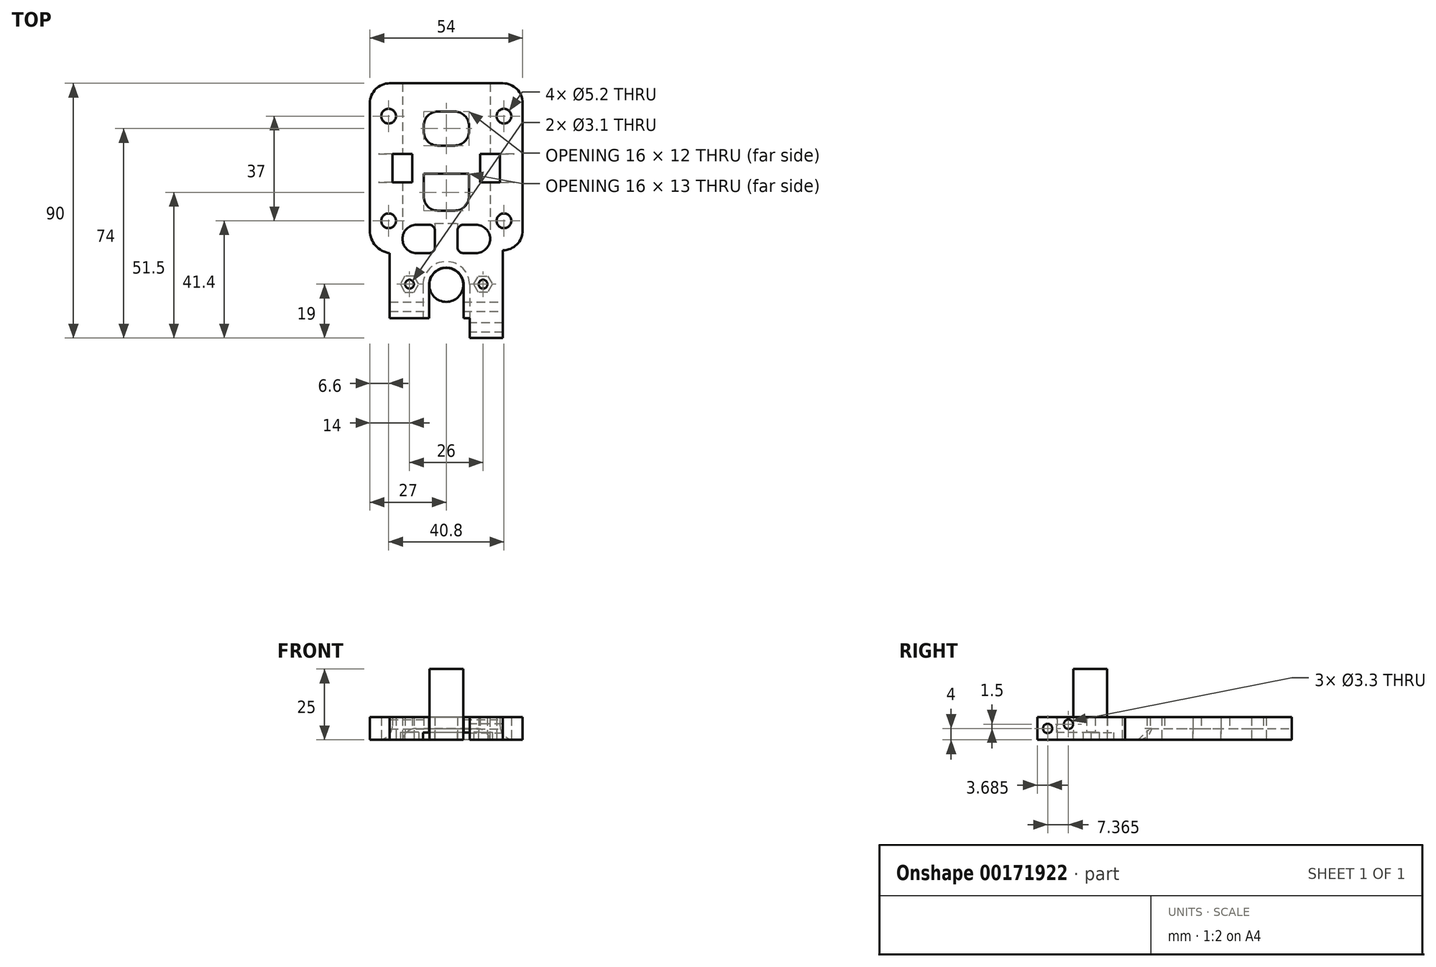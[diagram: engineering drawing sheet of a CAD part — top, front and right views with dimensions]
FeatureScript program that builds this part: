
annotation { "Feature Type Name" : "Feature", "Feature Type Description" : "" }
export const myFeature = defineFeature(function(context is Context, id is Id, definition is map)
    precondition{}
    {
        {
            var Q0;
            Q0=qCreatedBy(makeId("Top.planeOp"),FACE);
            var sketch = newSketch(context, id + "F0", { "sketchPlane" : qUnion([Q0])});
            skLineSegment(sketch, "E0.bottom", {"start": v(-27, 42.5) * mm, "end": v(27, 42.5) * mm});
            skLineSegment(sketch, "E0.top", {"start": v(-20, -42.5) * mm, "end": v(-6.1, -42.5) * mm});
            skLineSegment(sketch, "E0.left", {"start": v(-27, 42.5) * mm, "end": v(-27, -26.5) * mm});
            skLineSegment(sketch, "E0.right", {"start": v(27, 42.5) * mm, "end": v(27, -16.5) * mm});
            skPoint(sketch, "E0.middle", {"position": v(0, 0) * mm});
            skLineSegment(sketch, "E1.left", {"start": v(-20, -26.5) * mm, "end": v(-20, -42.5) * mm});
            skLineSegment(sketch, "E1.right", {"start": v(20, -16.5) * mm, "end": v(20, -42.5) * mm});
            skLineSegment(sketch, "E2", {"start": v(-20, -26.5) * mm, "end": v(-27, -26.5) * mm});
            skPoint(sketch, "E3.orphan", {"position": v(-27, -42.5) * mm});
            skLineSegment(sketch, "E4", {"start": v(20, -16.5) * mm, "end": v(27, -16.5) * mm});
            skPoint(sketch, "E5.orphan", {"position": v(27, -42.5) * mm});
            skCircle(sketch, "E6", {"center": v(-20.4, 30.9) * mm, "radius": 2.6 * mm});
            skCircle(sketch, "E7", {"center": v(-20.4, -6.1) * mm, "radius": 2.6 * mm});
            skCircle(sketch, "E8", {"center": v(20.4, 30.9) * mm, "radius": 2.6 * mm});
            skCircle(sketch, "E9.MirrorC", {"center": v(20.4, -6.1) * mm, "radius": 2.6 * mm});
            skLineSegment(sketch, "E10.bottom", {"start": v(-19, 17.5) * mm, "end": v(-12, 17.5) * mm});
            skLineSegment(sketch, "E10.top", {"start": v(-19, 7.5) * mm, "end": v(-12, 7.5) * mm});
            skLineSegment(sketch, "E10.left", {"start": v(-19, 17.5) * mm, "end": v(-19, 7.5) * mm});
            skLineSegment(sketch, "E10.right", {"start": v(-12, 17.5) * mm, "end": v(-12, 7.5) * mm});
            skLineSegment(sketch, "E11.MirrorCS", {"start": v(12, 17.5) * mm, "end": v(12, 7.5) * mm});
            skLineSegment(sketch, "E12.MirrorCS", {"start": v(19, 7.5) * mm, "end": v(12, 7.5) * mm});
            skLineSegment(sketch, "E13.MirrorCS", {"start": v(19, 17.5) * mm, "end": v(19, 7.5) * mm});
            skLineSegment(sketch, "E14.MirrorCS", {"start": v(19, 17.5) * mm, "end": v(12, 17.5) * mm});
            skEllipse(sketch, "E15", {"center": v(0, -13) * mm, "majorRadius": 7.5 * mm, "minorRadius": 4.5 * mm, "majorAxis": v(1, 0)});
            skArc(sketch, "E16", {"start": v(6.1, -28.75) * mm, "mid": v(0, -22.65) * mm, "end": v(-6.1, -28.75) * mm});
            skCircle(sketch, "E17", {"center": v(-12.5, -13) * mm, "radius": 2 * mm});
            skLineSegment(sketch, "E18", {"start": v(-6.1, -28.75) * mm, "end": v(-6.1, -42.5) * mm});
            skLineSegment(sketch, "E19", {"start": v(6.1, -28.75) * mm, "end": v(6.1, -42.5) * mm});
            skLineSegment(sketch, "E20.trimOffspring", {"start": v(6.1, -42.5) * mm, "end": v(20, -42.5) * mm});
            skArc(sketch, "E21", {"start": v(6.1, -34.3) * mm, "mid": v(0, -20.5) * mm, "end": v(-6.1, -34.3) * mm});
            skCircle(sketch, "E22", {"center": v(0, -28.75) * mm, "radius": 6 * mm});
            skSolve(sketch);
        }
        {
            var Q0;
            {var subQ0=sQuery(id+"F0.wireOp",EDGE,"E16");Q0=makeQuery(id+"F0.imprint","IMPRINT",FACE,{"disambiguationData":[TD([[makeQuery(id+"F0.imprint","IMPRINT",EDGE,{"derivedFrom":subQ0}),-1.0]])]});}
            var Q1;
            Q1=makeQuery(id+"F0.imprint","IMPRINT",FACE,{"disambiguationData":[TD([[makeQuery(id+"F0.imprint","IMPRINT",EDGE,{"derivedFrom":sQuery(id+"F0.wireOp",EDGE,"E0.bottom")}),-1.0]])]});
            extrude(context, id + "F1", {"entities" : qUnion([Q0, Q1]), "depth" : 8 * mm});
        }
        {
            var Q0;
            {var subQ0=sQuery(id+"F0.wireOp",EDGE,"E16");Q0=makeQuery(id+"F0.imprint","IMPRINT",FACE,{"disambiguationData":[TD([[makeQuery(id+"F0.imprint","IMPRINT",EDGE,{"derivedFrom":subQ0}),-1.0]])]});}
            extrude(context, id + "F2", {"entities" : qUnion([Q0]), "operationType" : NewBodyOperationType.REMOVE, "depth" : 2.6 * mm});
        }
        {
            var Q0;
            Q0=makeQuery(id+"F0.imprint","IMPRINT",FACE,{"disambiguationData":[TD([[makeQuery(id+"F0.imprint","IMPRINT",EDGE,{"derivedFrom":sQuery(id+"F0.wireOp",EDGE,"E22")}),1.0]])]});
            extrude(context, id + "F3", {"entities" : qUnion([Q0]), "depth" : 25 * mm});
        }
        {
            var Q0;
            Q0=qCreatedBy(makeId("Right.planeOp"),FACE);
            var sketch = newSketch(context, id + "F4", { "sketchPlane" : qUnion([Q0])});
            skCircle(sketch, "E23", {"center": v(-36.45, 5.5) * mm, "radius": 1.65 * mm});
            skLineSegment(sketch, "E24", {"start": v(-34.74, 0) * mm, "end": v(-34.74, 1.48) * mm});
            skSolve(sketch);
        }
        {
            var Q0;
            Q0=makeQuery(id+"F4.imprint","IMPRINT",FACE,{"disambiguationData":[TD([[makeQuery(id+"F4.imprint","IMPRINT",EDGE,{"derivedFrom":sQuery(id+"F4.wireOp",EDGE,"E23")}),1.0]])]});
            extrude(context, id + "F5", {"entities" : qUnion([Q0]), "operationType" : NewBodyOperationType.REMOVE, "endBound" : BoundingType.SYMMETRIC, "oppositeDirection" : true, "depth" : 100 * mm});
        }
        {
            var Q0;
            Q0=makeQuery(id+"F1.opExtrude","SWEPT_FACE",FACE,{"disambiguationData":[OSD([sQuery(id+"F0.wireOp",EDGE,"E20.trimOffspring")])]});
            extrude(context, id + "F6", {"entities" : qUnion([Q0]), "operationType" : NewBodyOperationType.ADD, "depth" : 5 * mm});
        }
        {
            var Q0;
            Q0=makeQuery(id+"F1.opExtrude","SWEPT_FACE",FACE,{"disambiguationData":[OSD([sQuery(id+"F0.wireOp",EDGE,"E0.top")])]});
            extrude(context, id + "F7", {"entities" : qUnion([Q0]), "operationType" : NewBodyOperationType.REMOVE, "oppositeDirection" : true, "depth" : 2 * mm});
        }
        {
            var Q0;
            {var subQ0=sQuery(id+"F0.wireOp",EDGE,"E20.trimOffspring");Q0=makeQuery(id+"F6.boolean.opBoolean","MERGE",FACE,{"derivedFrom":[makeQuery(id+"F1.opExtrude","CAP_FACE",FACE,{"disambiguationData":[OSD([sQuery(id+"F0.wireOp",EDGE,"E0.bottom"),sQuery(id+"F0.wireOp",EDGE,"E0.left"),sQuery(id+"F0.wireOp",EDGE,"E0.right"),sQuery(id+"F0.wireOp",EDGE,"E0.top"),sQuery(id+"F0.wireOp",EDGE,"E1.left"),sQuery(id+"F0.wireOp",EDGE,"E1.right"),sQuery(id+"F0.wireOp",EDGE,"E2"),sQuery(id+"F0.wireOp",EDGE,"E4"),sQuery(id+"F0.wireOp",EDGE,"E6"),sQuery(id+"F0.wireOp",EDGE,"E7"),sQuery(id+"F0.wireOp",EDGE,"E8"),sQuery(id+"F0.wireOp",EDGE,"E9.MirrorC"),sQuery(id+"F0.wireOp",EDGE,"E10.bottom"),sQuery(id+"F0.wireOp",EDGE,"E10.top"),sQuery(id+"F0.wireOp",EDGE,"E10.left"),sQuery(id+"F0.wireOp",EDGE,"E10.right"),sQuery(id+"F0.wireOp",EDGE,"E11.MirrorCS"),sQuery(id+"F0.wireOp",EDGE,"E12.MirrorCS"),sQuery(id+"F0.wireOp",EDGE,"E13.MirrorCS"),sQuery(id+"F0.wireOp",EDGE,"E14.MirrorCS"),sQuery(id+"F0.wireOp",EDGE,"E15"),sQuery(id+"F0.wireOp",EDGE,"E16"),sQuery(id+"F0.wireOp",EDGE,"E17"),sQuery(id+"F0.wireOp",EDGE,"E18"),sQuery(id+"F0.wireOp",EDGE,"E19"),subQ0])],"isStart":true}),makeQuery(id+"F6.opExtrude","SWEPT_FACE",FACE,{"disambiguationData":[OSD([subQ0]),TDD([makeQuery(id+"F1.opExtrude","CAP_EDGE",EDGE,{"disambiguationData":[OSD([subQ0])],"isStart":true})])]})]});}
            var sketch = newSketch(context, id + "F8", { "sketchPlane" : qUnion([Q0])});
            skLineSegment(sketch, "E25", {"start": v(8.25, 28.75) * mm, "end": v(8.25, 47.5) * mm});
            skLineSegment(sketch, "E26", {"start": v(-8.25, 28.75) * mm, "end": v(-8.25, 40.5) * mm});
            skLineSegment(sketch, "E27", {"start": v(0, 28.75) * mm, "end": v(8.25, 28.75) * mm});
            skLineSegment(sketch, "E28", {"start": v(0, 28.75) * mm, "end": v(-8.25, 28.75) * mm});
            skSolve(sketch);
        }
        {
            var Q0;
            {var subQ0=sQuery(id+"F8.wireOp",EDGE,"E25");Q0=makeQuery(id+"F8.imprint","IMPRINT",FACE,{"disambiguationData":[TD([[makeQuery(id+"F8.imprint","IMPRINT",EDGE,{"derivedFrom":subQ0}),1.0]])]});}
            var Q1;
            {var subQ0=sQuery(id+"F8.wireOp",EDGE,"E26");Q1=makeQuery(id+"F8.imprint","IMPRINT",FACE,{"disambiguationData":[TD([[makeQuery(id+"F8.imprint","IMPRINT",EDGE,{"derivedFrom":subQ0}),-1.0]])]});}
            var Q2;
            Q2=makeQuery(id+"F2.boolean.opBoolean","COPY",FACE,{"derivedFrom":makeQuery(id+"F2.opExtrude","CAP_FACE",FACE,{"disambiguationData":[OSD([sQuery(id+"F0.wireOp",EDGE,"E16"),sQuery(id+"F0.wireOp",EDGE,"E18"),sQuery(id+"F0.wireOp",EDGE,"E19"),sQuery(id+"F0.wireOp",EDGE,"E21")])],"isStart":false})});
            extrude(context, id + "F9", {"entities" : qUnion([Q0, Q1]), "operationType" : NewBodyOperationType.REMOVE, "endBound" : BoundingType.UP_TO_SURFACE, "oppositeDirection" : true, "endBoundEntityFace" : qUnion([Q2]), "depth" : 25 * mm});
        }
        {
            var Q0;
            {var subQ0=sQuery(id+"F0.wireOp",EDGE,"E19");Q0=makeQuery(id+"F6.boolean.opBoolean","MERGE",FACE,{"derivedFrom":[makeQuery(id+"F1.opExtrude","SWEPT_FACE",FACE,{"disambiguationData":[OSD([subQ0])]}),makeQuery(id+"F6.opExtrude","SWEPT_FACE",FACE,{"disambiguationData":[OSD([subQ0,sQuery(id+"F0.wireOp",EDGE,"E20.trimOffspring")])]})]});}
            var sketch = newSketch(context, id + "F10", { "sketchPlane" : qUnion([Q0])});
            skLineSegment(sketch, "E29.bottom", {"start": v(47.5, 2.6) * mm, "end": v(40.53, 2.6) * mm});
            skLineSegment(sketch, "E29.top", {"start": v(47.5, 8) * mm, "end": v(40.53, 8) * mm});
            skLineSegment(sketch, "E29.left", {"start": v(47.5, 2.6) * mm, "end": v(47.5, 8) * mm});
            skLineSegment(sketch, "E29.right", {"start": v(40.53, 2.6) * mm, "end": v(40.53, 8) * mm});
            skSolve(sketch);
        }
        {
            var Q0;
            Q0 = qSketchRegion(id + "F10", true);
            var Q1;
            Q1=makeQuery(id+"F9.boolean.opBoolean","COPY",FACE,{"derivedFrom":makeQuery(id+"F9.opExtrude","SWEPT_FACE",FACE,{"disambiguationData":[OSD([sQuery(id+"F8.wireOp",EDGE,"E25")])]})});
            extrude(context, id + "F11", {"entities" : qUnion([Q0]), "operationType" : NewBodyOperationType.REMOVE, "endBound" : BoundingType.UP_TO_SURFACE, "oppositeDirection" : true, "endBoundEntityFace" : qUnion([Q1]), "depth" : 25 * mm});
        }
        {
            var Q0;
            Q0=makeQuery(id+"F11.boolean.opBoolean","MERGE",FACE,{"derivedFrom":[makeQuery(id+"F9.boolean.opBoolean","COPY",FACE,{"derivedFrom":makeQuery(id+"F9.opExtrude","SWEPT_FACE",FACE,{"disambiguationData":[OSD([sQuery(id+"F8.wireOp",EDGE,"E25")])]})})],"fromTools":[makeQuery(id+"F11.opExtrude","CAP_FACE",FACE,{"disambiguationData":[OSD([sQuery(id+"F10.wireOp",EDGE,"E29.bottom"),sQuery(id+"F10.wireOp",EDGE,"E29.top"),sQuery(id+"F10.wireOp",EDGE,"E29.left"),sQuery(id+"F10.wireOp",EDGE,"E29.right")])],"isStart":false})]});
            var sketch = newSketch(context, id + "F12", { "sketchPlane" : qUnion([Q0])});
            skCircle(sketch, "E30", {"center": v(43.82, 4) * mm, "radius": 1.65 * mm});
            skPoint(sketch, "E30.centerSnap0", {"position": v(47.5, 4) * mm});
            skSolve(sketch);
        }
        {
            var Q0;
            Q0=makeQuery(id+"F12.imprint","IMPRINT",FACE,{"disambiguationData":[TD([[makeQuery(id+"F12.imprint","IMPRINT",EDGE,{"derivedFrom":sQuery(id+"F12.wireOp",EDGE,"E30")}),1.0]])]});
            extrude(context, id + "F13", {"entities" : qUnion([Q0]), "operationType" : NewBodyOperationType.REMOVE, "oppositeDirection" : true, "depth" : 25 * mm});
        }
        {
            var Q0;
            {var subQ0=sQuery(id+"F0.wireOp",EDGE,"E20.trimOffspring");Q0=makeQuery(id+"F6.boolean.opBoolean","MERGE",FACE,{"derivedFrom":[makeQuery(id+"F1.opExtrude","CAP_FACE",FACE,{"disambiguationData":[OSD([sQuery(id+"F0.wireOp",EDGE,"E0.bottom"),sQuery(id+"F0.wireOp",EDGE,"E0.left"),sQuery(id+"F0.wireOp",EDGE,"E0.right"),sQuery(id+"F0.wireOp",EDGE,"E0.top"),sQuery(id+"F0.wireOp",EDGE,"E1.left"),sQuery(id+"F0.wireOp",EDGE,"E1.right"),sQuery(id+"F0.wireOp",EDGE,"E2"),sQuery(id+"F0.wireOp",EDGE,"E4"),sQuery(id+"F0.wireOp",EDGE,"E6"),sQuery(id+"F0.wireOp",EDGE,"E7"),sQuery(id+"F0.wireOp",EDGE,"E8"),sQuery(id+"F0.wireOp",EDGE,"E9.MirrorC"),sQuery(id+"F0.wireOp",EDGE,"E10.bottom"),sQuery(id+"F0.wireOp",EDGE,"E10.top"),sQuery(id+"F0.wireOp",EDGE,"E10.left"),sQuery(id+"F0.wireOp",EDGE,"E10.right"),sQuery(id+"F0.wireOp",EDGE,"E11.MirrorCS"),sQuery(id+"F0.wireOp",EDGE,"E12.MirrorCS"),sQuery(id+"F0.wireOp",EDGE,"E13.MirrorCS"),sQuery(id+"F0.wireOp",EDGE,"E14.MirrorCS"),sQuery(id+"F0.wireOp",EDGE,"E15"),sQuery(id+"F0.wireOp",EDGE,"E16"),sQuery(id+"F0.wireOp",EDGE,"E17"),sQuery(id+"F0.wireOp",EDGE,"E18"),sQuery(id+"F0.wireOp",EDGE,"E19"),subQ0])],"isStart":true}),makeQuery(id+"F6.opExtrude","SWEPT_FACE",FACE,{"disambiguationData":[OSD([subQ0]),TDD([makeQuery(id+"F1.opExtrude","CAP_EDGE",EDGE,{"disambiguationData":[OSD([subQ0])],"isStart":true})])]})]});}
            var sketch = newSketch(context, id + "F14", { "sketchPlane" : qUnion([Q0])});
            skCircle(sketch, "E31.cCircle", {"center": v(-13, 28.5) * mm, "radius": 2.85 * mm, "construction": true});
            skLineSegment(sketch, "E31.0", {"start": v(-11.35, 25.65) * mm, "end": v(-14.65, 25.65) * mm});
            skLineSegment(sketch, "E31.1", {"start": v(-14.65, 25.65) * mm, "end": v(-16.3, 28.5) * mm});
            skLineSegment(sketch, "E31.2", {"start": v(-16.3, 28.5) * mm, "end": v(-14.65, 31.35) * mm});
            skLineSegment(sketch, "E31.3", {"start": v(-14.65, 31.35) * mm, "end": v(-11.35, 31.35) * mm});
            skLineSegment(sketch, "E31.4", {"start": v(-11.35, 31.35) * mm, "end": v(-9.7, 28.5) * mm});
            skLineSegment(sketch, "E31.5", {"start": v(-9.7, 28.5) * mm, "end": v(-11.35, 25.65) * mm});
            skPoint(sketch, "E31.0.midPoint", {"position": v(-13, 25.65) * mm});
            skLineSegment(sketch, "E32.MirrorCS", {"start": v(9.7, 28.5) * mm, "end": v(11.35, 25.65) * mm});
            skLineSegment(sketch, "E33.MirrorCS", {"start": v(11.35, 31.35) * mm, "end": v(9.7, 28.5) * mm});
            skLineSegment(sketch, "E34.MirrorCS", {"start": v(14.65, 31.35) * mm, "end": v(11.35, 31.35) * mm});
            skPoint(sketch, "E35.MirrorP", {"position": v(13, 25.65) * mm});
            skCircle(sketch, "E36.MirrorC", {"center": v(13, 28.5) * mm, "radius": 2.85 * mm, "construction": true});
            skLineSegment(sketch, "E37.MirrorCS", {"start": v(11.35, 25.65) * mm, "end": v(14.65, 25.65) * mm});
            skLineSegment(sketch, "E38.MirrorCS", {"start": v(14.65, 25.65) * mm, "end": v(16.3, 28.5) * mm});
            skLineSegment(sketch, "E39.MirrorCS", {"start": v(16.3, 28.5) * mm, "end": v(14.65, 31.35) * mm});
            skCircle(sketch, "E40", {"center": v(-13, 28.5) * mm, "radius": 1.55 * mm});
            skCircle(sketch, "E41.MirrorC", {"center": v(13, 28.5) * mm, "radius": 1.55 * mm});
            skSolve(sketch);
        }
        {
            var Q0;
            Q0 = qSketchRegion(id + "F14", true);
            extrude(context, id + "F15", {"entities" : qUnion([Q0]), "operationType" : NewBodyOperationType.REMOVE, "oppositeDirection" : true, "depth" : 2.7 * mm});
        }
        {
            var Q0;
            {var subQ0=sQuery(id+"F0.wireOp",EDGE,"E20.trimOffspring");Q0=makeQuery(id+"F15.boolean.opBoolean","SPLIT",FACE,{"disambiguationData":[TD([makeQuery(id+"F15.opExtrude","SWEPT_FACE",FACE,{"disambiguationData":[OSD([sQuery(id+"F14.wireOp",EDGE,"E40")])]})])],"derivedFrom":makeQuery(id+"F6.boolean.opBoolean","MERGE",FACE,{"derivedFrom":[makeQuery(id+"F1.opExtrude","CAP_FACE",FACE,{"disambiguationData":[OSD([sQuery(id+"F0.wireOp",EDGE,"E0.bottom"),sQuery(id+"F0.wireOp",EDGE,"E0.left"),sQuery(id+"F0.wireOp",EDGE,"E0.right"),sQuery(id+"F0.wireOp",EDGE,"E0.top"),sQuery(id+"F0.wireOp",EDGE,"E1.left"),sQuery(id+"F0.wireOp",EDGE,"E1.right"),sQuery(id+"F0.wireOp",EDGE,"E2"),sQuery(id+"F0.wireOp",EDGE,"E4"),sQuery(id+"F0.wireOp",EDGE,"E6"),sQuery(id+"F0.wireOp",EDGE,"E7"),sQuery(id+"F0.wireOp",EDGE,"E8"),sQuery(id+"F0.wireOp",EDGE,"E9.MirrorC"),sQuery(id+"F0.wireOp",EDGE,"E10.bottom"),sQuery(id+"F0.wireOp",EDGE,"E10.top"),sQuery(id+"F0.wireOp",EDGE,"E10.left"),sQuery(id+"F0.wireOp",EDGE,"E10.right"),sQuery(id+"F0.wireOp",EDGE,"E11.MirrorCS"),sQuery(id+"F0.wireOp",EDGE,"E12.MirrorCS"),sQuery(id+"F0.wireOp",EDGE,"E13.MirrorCS"),sQuery(id+"F0.wireOp",EDGE,"E14.MirrorCS"),sQuery(id+"F0.wireOp",EDGE,"E15"),sQuery(id+"F0.wireOp",EDGE,"E16"),sQuery(id+"F0.wireOp",EDGE,"E17"),sQuery(id+"F0.wireOp",EDGE,"E18"),sQuery(id+"F0.wireOp",EDGE,"E19"),subQ0])],"isStart":true}),makeQuery(id+"F6.opExtrude","SWEPT_FACE",FACE,{"disambiguationData":[OSD([subQ0]),TDD([makeQuery(id+"F1.opExtrude","CAP_EDGE",EDGE,{"disambiguationData":[OSD([subQ0])],"isStart":true})])]})]})});}
            var Q1;
            {var subQ0=sQuery(id+"F0.wireOp",EDGE,"E20.trimOffspring");Q1=makeQuery(id+"F15.boolean.opBoolean","SPLIT",FACE,{"disambiguationData":[TD([makeQuery(id+"F15.opExtrude","SWEPT_FACE",FACE,{"disambiguationData":[OSD([sQuery(id+"F14.wireOp",EDGE,"E41.MirrorC")])]})])],"derivedFrom":makeQuery(id+"F6.boolean.opBoolean","MERGE",FACE,{"derivedFrom":[makeQuery(id+"F1.opExtrude","CAP_FACE",FACE,{"disambiguationData":[OSD([sQuery(id+"F0.wireOp",EDGE,"E0.bottom"),sQuery(id+"F0.wireOp",EDGE,"E0.left"),sQuery(id+"F0.wireOp",EDGE,"E0.right"),sQuery(id+"F0.wireOp",EDGE,"E0.top"),sQuery(id+"F0.wireOp",EDGE,"E1.left"),sQuery(id+"F0.wireOp",EDGE,"E1.right"),sQuery(id+"F0.wireOp",EDGE,"E2"),sQuery(id+"F0.wireOp",EDGE,"E4"),sQuery(id+"F0.wireOp",EDGE,"E6"),sQuery(id+"F0.wireOp",EDGE,"E7"),sQuery(id+"F0.wireOp",EDGE,"E8"),sQuery(id+"F0.wireOp",EDGE,"E9.MirrorC"),sQuery(id+"F0.wireOp",EDGE,"E10.bottom"),sQuery(id+"F0.wireOp",EDGE,"E10.top"),sQuery(id+"F0.wireOp",EDGE,"E10.left"),sQuery(id+"F0.wireOp",EDGE,"E10.right"),sQuery(id+"F0.wireOp",EDGE,"E11.MirrorCS"),sQuery(id+"F0.wireOp",EDGE,"E12.MirrorCS"),sQuery(id+"F0.wireOp",EDGE,"E13.MirrorCS"),sQuery(id+"F0.wireOp",EDGE,"E14.MirrorCS"),sQuery(id+"F0.wireOp",EDGE,"E15"),sQuery(id+"F0.wireOp",EDGE,"E16"),sQuery(id+"F0.wireOp",EDGE,"E17"),sQuery(id+"F0.wireOp",EDGE,"E18"),sQuery(id+"F0.wireOp",EDGE,"E19"),subQ0])],"isStart":true}),makeQuery(id+"F6.opExtrude","SWEPT_FACE",FACE,{"disambiguationData":[OSD([subQ0]),TDD([makeQuery(id+"F1.opExtrude","CAP_EDGE",EDGE,{"disambiguationData":[OSD([subQ0])],"isStart":true})])]})]})});}
            extrude(context, id + "F16", {"entities" : qUnion([Q0, Q1]), "operationType" : NewBodyOperationType.REMOVE, "oppositeDirection" : true, "depth" : 25 * mm});
        }
        {
            var Q0;
            Q0=makeQuery(id+"F1.opExtrude","SWEPT_EDGE",EDGE,{"disambiguationData":[OSD([sQuery(id+"F0.wireOp",EDGE,"E0.bottom"),sQuery(id+"F0.wireOp",EDGE,"E0.right")])]});
            var Q1;
            Q1=makeQuery(id+"F1.opExtrude","SWEPT_EDGE",EDGE,{"disambiguationData":[OSD([sQuery(id+"F0.wireOp",EDGE,"E0.bottom"),sQuery(id+"F0.wireOp",EDGE,"E0.left")])]});
            var Q2;
            Q2=makeQuery(id+"F1.opExtrude","SWEPT_EDGE",EDGE,{"disambiguationData":[OSD([sQuery(id+"F0.wireOp",EDGE,"E0.left"),sQuery(id+"F0.wireOp",EDGE,"E2")])]});
            var Q3;
            Q3=makeQuery(id+"F1.opExtrude","SWEPT_EDGE",EDGE,{"disambiguationData":[OSD([sQuery(id+"F0.wireOp",EDGE,"E0.right"),sQuery(id+"F0.wireOp",EDGE,"E4")])]});
            fillet(context, id + "F17", {"entities" : qUnion([Q0, Q1, Q2, Q3]), "radius" : 7 * mm, "tangentPropagation" : true, "allowEdgeOverflow" : false});
        }
        {
            var Q0;
            {var subQ0=sQuery(id+"F0.wireOp",EDGE,"E17");var subQ1=sQuery(id+"F0.wireOp",EDGE,"E15");var subQ2=sQuery(id+"F0.wireOp",EDGE,"E14.MirrorCS");var subQ3=sQuery(id+"F0.wireOp",EDGE,"E13.MirrorCS");var subQ4=sQuery(id+"F0.wireOp",EDGE,"E0.right");var subQ5=sQuery(id+"F0.wireOp",EDGE,"E12.MirrorCS");var subQ6=sQuery(id+"F0.wireOp",EDGE,"E11.MirrorCS");var subQ7=sQuery(id+"F0.wireOp",EDGE,"E0.top");var subQ8=sQuery(id+"F0.wireOp",EDGE,"E10.right");var subQ9=sQuery(id+"F0.wireOp",EDGE,"E10.left");var subQ10=sQuery(id+"F0.wireOp",EDGE,"E10.top");var subQ11=sQuery(id+"F0.wireOp",EDGE,"E10.bottom");var subQ12=sQuery(id+"F0.wireOp",EDGE,"E9.MirrorC");var subQ13=sQuery(id+"F0.wireOp",EDGE,"E1.left");var subQ14=sQuery(id+"F0.wireOp",EDGE,"E0.left");var subQ15=sQuery(id+"F0.wireOp",EDGE,"E0.bottom");var subQ16=sQuery(id+"F0.wireOp",EDGE,"E7");var subQ17=sQuery(id+"F0.wireOp",EDGE,"E1.right");var subQ18=sQuery(id+"F0.wireOp",EDGE,"E2");var subQ19=sQuery(id+"F0.wireOp",EDGE,"E4");var subQ20=sQuery(id+"F0.wireOp",EDGE,"E6");var subQ21=sQuery(id+"F0.wireOp",EDGE,"E8");var subQ22=sQuery(id+"F0.wireOp",EDGE,"E20.trimOffspring");Q0=makeQuery(id+"F15.boolean.opBoolean","SPLIT",FACE,{"disambiguationData":[TD([makeQuery(id+"F1.opExtrude","SWEPT_FACE",FACE,{"disambiguationData":[OSD([subQ15])]})])],"derivedFrom":makeQuery(id+"F6.boolean.opBoolean","MERGE",FACE,{"derivedFrom":[makeQuery(id+"F1.opExtrude","CAP_FACE",FACE,{"disambiguationData":[OSD([subQ15,subQ14,subQ4,subQ7,subQ13,subQ17,subQ18,subQ19,subQ20,subQ16,subQ21,subQ12,subQ11,subQ10,subQ9,subQ8,subQ6,subQ5,subQ3,subQ2,subQ1,sQuery(id+"F0.wireOp",EDGE,"E16"),subQ0,sQuery(id+"F0.wireOp",EDGE,"E18"),sQuery(id+"F0.wireOp",EDGE,"E19"),subQ22])],"isStart":true}),makeQuery(id+"F6.opExtrude","SWEPT_FACE",FACE,{"disambiguationData":[OSD([subQ22]),TDD([makeQuery(id+"F1.opExtrude","CAP_EDGE",EDGE,{"disambiguationData":[OSD([subQ22])],"isStart":true})])]})]})});}
            var sketch = newSketch(context, id + "F18", { "sketchPlane" : qUnion([Q0])});
            skLineSegment(sketch, "E42.bottom", {"start": v(8, -32.5) * mm, "end": v(-8, -32.5) * mm});
            skLineSegment(sketch, "E42.top", {"start": v(8, 2.5) * mm, "end": v(-8, 2.5) * mm});
            skLineSegment(sketch, "E42.left", {"start": v(8, -32.5) * mm, "end": v(8, 2.5) * mm});
            skLineSegment(sketch, "E42.right", {"start": v(-8, -32.5) * mm, "end": v(-8, 2.5) * mm});
            skPoint(sketch, "E42.middle", {"position": v(0, -15) * mm});
            skSolve(sketch);
        }
        {
            var Q0;
            Q0 = qSketchRegion(id + "F18", true);
            extrude(context, id + "F19", {"entities" : qUnion([Q0]), "operationType" : NewBodyOperationType.REMOVE, "oppositeDirection" : true, "depth" : 25 * mm});
        }
        {
            var Q0;
            Q0=makeQuery(id+"F19.boolean.opBoolean","COPY",FACE,{"derivedFrom":makeQuery(id+"F19.opExtrude","SWEPT_FACE",FACE,{"disambiguationData":[OSD([sQuery(id+"F18.wireOp",EDGE,"E42.right")])]})});
            var sketch = newSketch(context, id + "F20", { "sketchPlane" : qUnion([Q0])});
            skLineSegment(sketch, "E43.bottom", {"start": v(10.5, 8) * mm, "end": v(20.5, 8) * mm});
            skLineSegment(sketch, "E43.top", {"start": v(10.5, 0) * mm, "end": v(20.5, 0) * mm});
            skLineSegment(sketch, "E43.left", {"start": v(10.5, 8) * mm, "end": v(10.5, 0) * mm});
            skLineSegment(sketch, "E43.right", {"start": v(20.5, 8) * mm, "end": v(20.5, 0) * mm});
            skSolve(sketch);
        }
        {
            var Q0;
            Q0 = qSketchRegion(id + "F20", true);
            extrude(context, id + "F21", {"entities" : qUnion([Q0]), "operationType" : NewBodyOperationType.ADD, "endBound" : BoundingType.UP_TO_NEXT, "depth" : 25 * mm});
        }
        {
            var Q0;
            Q0=makeQuery(id+"F21.opExtrude","CAP_EDGE",EDGE,{"disambiguationData":[OSD([sQuery(id+"F20.wireOp",EDGE,"E43.left")])],"isStart":true});
            var Q1;
            Q1=makeQuery(id+"F19.boolean.opBoolean","COPY",EDGE,{"derivedFrom":makeQuery(id+"F19.opExtrude","SWEPT_EDGE",EDGE,{"disambiguationData":[OSD([sQuery(id+"F18.wireOp",EDGE,"E42.top"),sQuery(id+"F18.wireOp",EDGE,"E42.right")])]})});
            var Q2;
            Q2=makeQuery(id+"F19.boolean.opBoolean","COPY",EDGE,{"derivedFrom":makeQuery(id+"F19.opExtrude","SWEPT_EDGE",EDGE,{"disambiguationData":[OSD([sQuery(id+"F18.wireOp",EDGE,"E42.top"),sQuery(id+"F18.wireOp",EDGE,"E42.left")])]})});
            var Q3;
            Q3=makeQuery(id+"F21.opExtrude","CAP_EDGE",EDGE,{"disambiguationData":[OSD([sQuery(id+"F20.wireOp",EDGE,"E43.left")])],"isStart":false});
            var Q4;
            Q4=makeQuery(id+"F21.opExtrude","CAP_EDGE",EDGE,{"disambiguationData":[OSD([sQuery(id+"F20.wireOp",EDGE,"E43.right")])],"isStart":false});
            var Q5;
            Q5=makeQuery(id+"F21.opExtrude","CAP_EDGE",EDGE,{"disambiguationData":[OSD([sQuery(id+"F20.wireOp",EDGE,"E43.right")])],"isStart":true});
            var Q6;
            Q6=makeQuery(id+"F19.boolean.opBoolean","COPY",EDGE,{"derivedFrom":makeQuery(id+"F19.opExtrude","SWEPT_EDGE",EDGE,{"disambiguationData":[OSD([sQuery(id+"F18.wireOp",EDGE,"E42.bottom"),sQuery(id+"F18.wireOp",EDGE,"E42.right")])]})});
            var Q7;
            Q7=makeQuery(id+"F19.boolean.opBoolean","COPY",EDGE,{"derivedFrom":makeQuery(id+"F19.opExtrude","SWEPT_EDGE",EDGE,{"disambiguationData":[OSD([sQuery(id+"F18.wireOp",EDGE,"E42.bottom"),sQuery(id+"F18.wireOp",EDGE,"E42.left")])]})});
            fillet(context, id + "F22", {"entities" : qUnion([Q0, Q1, Q2, Q3, Q4, Q5, Q6, Q7]), "radius" : 5 * mm, "tangentPropagation" : true, "allowEdgeOverflow" : false});
        }
        {
            var Q0;
            {var subQ0=sQuery(id+"F0.wireOp",EDGE,"E17");var subQ1=sQuery(id+"F0.wireOp",EDGE,"E15");var subQ2=sQuery(id+"F0.wireOp",EDGE,"E14.MirrorCS");var subQ3=sQuery(id+"F0.wireOp",EDGE,"E13.MirrorCS");var subQ4=sQuery(id+"F0.wireOp",EDGE,"E0.right");var subQ5=sQuery(id+"F0.wireOp",EDGE,"E12.MirrorCS");var subQ6=sQuery(id+"F0.wireOp",EDGE,"E11.MirrorCS");var subQ7=sQuery(id+"F0.wireOp",EDGE,"E0.top");var subQ8=sQuery(id+"F0.wireOp",EDGE,"E10.right");var subQ9=sQuery(id+"F0.wireOp",EDGE,"E10.left");var subQ10=sQuery(id+"F0.wireOp",EDGE,"E10.top");var subQ11=sQuery(id+"F0.wireOp",EDGE,"E10.bottom");var subQ12=sQuery(id+"F0.wireOp",EDGE,"E9.MirrorC");var subQ13=sQuery(id+"F0.wireOp",EDGE,"E1.left");var subQ14=sQuery(id+"F0.wireOp",EDGE,"E0.left");var subQ15=sQuery(id+"F0.wireOp",EDGE,"E0.bottom");var subQ16=sQuery(id+"F0.wireOp",EDGE,"E7");var subQ17=sQuery(id+"F0.wireOp",EDGE,"E1.right");var subQ18=sQuery(id+"F0.wireOp",EDGE,"E2");var subQ19=sQuery(id+"F0.wireOp",EDGE,"E4");var subQ20=sQuery(id+"F0.wireOp",EDGE,"E6");var subQ21=sQuery(id+"F0.wireOp",EDGE,"E8");var subQ22=sQuery(id+"F0.wireOp",EDGE,"E20.trimOffspring");Q0=makeQuery(id+"F21.boolean.opBoolean","MERGE",FACE,{"derivedFrom":[makeQuery(id+"F15.boolean.opBoolean","SPLIT",FACE,{"disambiguationData":[TD([makeQuery(id+"F1.opExtrude","SWEPT_FACE",FACE,{"disambiguationData":[OSD([subQ15])]})])],"derivedFrom":makeQuery(id+"F6.boolean.opBoolean","MERGE",FACE,{"derivedFrom":[makeQuery(id+"F1.opExtrude","CAP_FACE",FACE,{"disambiguationData":[OSD([subQ15,subQ14,subQ4,subQ7,subQ13,subQ17,subQ18,subQ19,subQ20,subQ16,subQ21,subQ12,subQ11,subQ10,subQ9,subQ8,subQ6,subQ5,subQ3,subQ2,subQ1,sQuery(id+"F0.wireOp",EDGE,"E16"),subQ0,sQuery(id+"F0.wireOp",EDGE,"E18"),sQuery(id+"F0.wireOp",EDGE,"E19"),subQ22])],"isStart":true}),makeQuery(id+"F6.opExtrude","SWEPT_FACE",FACE,{"disambiguationData":[OSD([subQ22]),TDD([makeQuery(id+"F1.opExtrude","CAP_EDGE",EDGE,{"disambiguationData":[OSD([subQ22])],"isStart":true})])]})]})}),makeQuery(id+"F21.opExtrude","SWEPT_FACE",FACE,{"disambiguationData":[OSD([sQuery(id+"F20.wireOp",EDGE,"E43.top")])]})]});}
            var sketch = newSketch(context, id + "F23", { "sketchPlane" : qUnion([Q0])});
            skPoint(sketch, "E44.oppositeSnap0", {"position": v(15.5, -7.5) * mm});
            skLineSegment(sketch, "E44.bottom", {"start": v(-15.5, -42.5) * mm, "end": v(15.5, -42.5) * mm});
            skLineSegment(sketch, "E44.top", {"start": v(-15.5, 17.5) * mm, "end": v(15.5, 17.5) * mm});
            skLineSegment(sketch, "E44.left", {"start": v(-15.5, -42.5) * mm, "end": v(-15.5, 17.5) * mm});
            skLineSegment(sketch, "E44.right", {"start": v(15.5, -42.5) * mm, "end": v(15.5, 17.5) * mm});
            skSolve(sketch);
        }
        {
            var Q0;
            Q0 = qSketchRegion(id + "F23", true);
            extrude(context, id + "F24", {"entities" : qUnion([Q0]), "operationType" : NewBodyOperationType.REMOVE, "oppositeDirection" : true, "depth" : 4 * mm});
        }
        {
            var Q0;
            Q0=makeQuery(id+"F24.boolean.opBoolean","COPY",FACE,{"derivedFrom":makeQuery(id+"F24.opExtrude","CAP_FACE",FACE,{"disambiguationData":[OSD([sQuery(id+"F23.wireOp",EDGE,"E44.bottom"),sQuery(id+"F23.wireOp",EDGE,"E44.top"),sQuery(id+"F23.wireOp",EDGE,"E44.left"),sQuery(id+"F23.wireOp",EDGE,"E44.right")])],"isStart":false})});
            var sketch = newSketch(context, id + "F25", { "sketchPlane" : qUnion([Q0])});
            skLineSegment(sketch, "E45.bottom", {"start": v(-15.5, 17.5) * mm, "end": v(15.5, 17.5) * mm});
            skLineSegment(sketch, "E45.top", {"start": v(-15.5, 7.5) * mm, "end": v(15.5, 7.5) * mm});
            skLineSegment(sketch, "E45.left", {"start": v(-15.5, 17.5) * mm, "end": v(-15.5, 7.5) * mm});
            skLineSegment(sketch, "E45.right", {"start": v(15.5, 17.5) * mm, "end": v(15.5, 7.5) * mm});
            skSolve(sketch);
        }
        {
            var Q0;
            Q0 = qSketchRegion(id + "F25", true);
            extrude(context, id + "F26", {"entities" : qUnion([Q0]), "operationType" : NewBodyOperationType.REMOVE, "oppositeDirection" : true, "depth" : 25 * mm});
        }
        {
            var Q0;
            Q0=makeQuery(id+"F1.opExtrude","CAP_EDGE",EDGE,{"disambiguationData":[OSD([sQuery(id+"F0.wireOp",EDGE,"E10.left")])],"isStart":true});
            var Q1;
            Q1=makeQuery(id+"F1.opExtrude","CAP_EDGE",EDGE,{"disambiguationData":[OSD([sQuery(id+"F0.wireOp",EDGE,"E13.MirrorCS")])],"isStart":true});
            fillet(context, id + "F27", {"entities" : qUnion([Q0, Q1]), "radius" : 5 * mm, "tangentPropagation" : true, "allowEdgeOverflow" : false});
        }
        {
            var Q0;
            {var subQ0=sQuery(id+"F23.wireOp",EDGE,"E44.left");Q0=makeQuery(id+"F24.boolean.opBoolean","COPY",EDGE,{"disambiguationData":[TD([makeQuery(id+"F1.opExtrude","SWEPT_FACE",FACE,{"disambiguationData":[OSD([sQuery(id+"F0.wireOp",EDGE,"E10.top")])]})])],"derivedFrom":makeQuery(id+"F24.opExtrude","CAP_EDGE",EDGE,{"disambiguationData":[OSD([subQ0])],"isStart":false})});}
            var Q1;
            {var subQ0=sQuery(id+"F23.wireOp",EDGE,"E44.right");Q1=makeQuery(id+"F24.boolean.opBoolean","COPY",EDGE,{"disambiguationData":[TD([makeQuery(id+"F1.opExtrude","SWEPT_FACE",FACE,{"disambiguationData":[OSD([sQuery(id+"F0.wireOp",EDGE,"E12.MirrorCS")])]})])],"derivedFrom":makeQuery(id+"F24.opExtrude","CAP_EDGE",EDGE,{"disambiguationData":[OSD([subQ0])],"isStart":false})});}
            fillet(context, id + "F28", {"entities" : qUnion([Q0, Q1]), "radius" : 5 * mm, "tangentPropagation" : true, "allowEdgeOverflow" : false});
        }
        {
            var Q0;
            Q0=makeQuery(id+"F26.boolean.opBoolean","COPY",EDGE,{"derivedFrom":makeQuery(id+"F26.opExtrude","SWEPT_EDGE",EDGE,{"disambiguationData":[OSD([sQuery(id+"F23.wireOp",EDGE,"E44.left"),sQuery(id+"F25.wireOp",EDGE,"E45.top"),sQuery(id+"F25.wireOp",EDGE,"E45.left")])]})});
            var Q1;
            Q1=makeQuery(id+"F26.boolean.opBoolean","COPY",EDGE,{"derivedFrom":makeQuery(id+"F26.opExtrude","SWEPT_EDGE",EDGE,{"disambiguationData":[OSD([sQuery(id+"F23.wireOp",EDGE,"E44.right"),sQuery(id+"F25.wireOp",EDGE,"E45.top"),sQuery(id+"F25.wireOp",EDGE,"E45.right")])]})});
            var Q2;
            Q2=makeQuery(id+"F26.boolean.opBoolean","MERGE",EDGE,{"derivedFrom":[makeQuery(id+"F24.boolean.opBoolean","COPY",EDGE,{"derivedFrom":makeQuery(id+"F24.opExtrude","SWEPT_EDGE",EDGE,{"disambiguationData":[OSD([sQuery(id+"F23.wireOp",EDGE,"E44.top"),sQuery(id+"F23.wireOp",EDGE,"E44.right")])]})}),makeQuery(id+"F26.opExtrude","SWEPT_EDGE",EDGE,{"disambiguationData":[OSD([sQuery(id+"F25.wireOp",EDGE,"E45.bottom"),sQuery(id+"F25.wireOp",EDGE,"E45.right")])]})]});
            var Q3;
            Q3=makeQuery(id+"F26.boolean.opBoolean","MERGE",EDGE,{"derivedFrom":[makeQuery(id+"F24.boolean.opBoolean","COPY",EDGE,{"derivedFrom":makeQuery(id+"F24.opExtrude","SWEPT_EDGE",EDGE,{"disambiguationData":[OSD([sQuery(id+"F23.wireOp",EDGE,"E44.top"),sQuery(id+"F23.wireOp",EDGE,"E44.left")])]})}),makeQuery(id+"F26.opExtrude","SWEPT_EDGE",EDGE,{"disambiguationData":[OSD([sQuery(id+"F25.wireOp",EDGE,"E45.bottom"),sQuery(id+"F25.wireOp",EDGE,"E45.left")])]})]});
            fillet(context, id + "F29", {"entities" : qUnion([Q0, Q1, Q2, Q3]), "radius" : 5 * mm, "tangentPropagation" : true, "allowEdgeOverflow" : false});
        }
        {
            var Q0;
            {var subQ0=sQuery(id+"F0.wireOp",EDGE,"E17");var subQ1=sQuery(id+"F0.wireOp",EDGE,"E15");var subQ2=sQuery(id+"F0.wireOp",EDGE,"E14.MirrorCS");var subQ3=sQuery(id+"F0.wireOp",EDGE,"E13.MirrorCS");var subQ4=sQuery(id+"F0.wireOp",EDGE,"E0.right");var subQ5=sQuery(id+"F0.wireOp",EDGE,"E12.MirrorCS");var subQ6=sQuery(id+"F0.wireOp",EDGE,"E11.MirrorCS");var subQ7=sQuery(id+"F0.wireOp",EDGE,"E0.top");var subQ8=sQuery(id+"F0.wireOp",EDGE,"E10.right");var subQ9=sQuery(id+"F0.wireOp",EDGE,"E10.left");var subQ10=sQuery(id+"F0.wireOp",EDGE,"E10.top");var subQ11=sQuery(id+"F0.wireOp",EDGE,"E10.bottom");var subQ12=sQuery(id+"F0.wireOp",EDGE,"E9.MirrorC");var subQ13=sQuery(id+"F0.wireOp",EDGE,"E1.left");var subQ14=sQuery(id+"F0.wireOp",EDGE,"E0.left");var subQ15=sQuery(id+"F0.wireOp",EDGE,"E0.bottom");var subQ16=sQuery(id+"F0.wireOp",EDGE,"E7");var subQ17=sQuery(id+"F0.wireOp",EDGE,"E1.right");var subQ18=sQuery(id+"F0.wireOp",EDGE,"E2");var subQ19=sQuery(id+"F0.wireOp",EDGE,"E4");var subQ20=sQuery(id+"F0.wireOp",EDGE,"E6");var subQ21=sQuery(id+"F0.wireOp",EDGE,"E8");var subQ22=sQuery(id+"F0.wireOp",EDGE,"E20.trimOffspring");Q0=makeQuery(id+"F21.boolean.opBoolean","MERGE",FACE,{"derivedFrom":[makeQuery(id+"F15.boolean.opBoolean","SPLIT",FACE,{"disambiguationData":[TD([makeQuery(id+"F1.opExtrude","SWEPT_FACE",FACE,{"disambiguationData":[OSD([subQ15])]})])],"derivedFrom":makeQuery(id+"F6.boolean.opBoolean","MERGE",FACE,{"derivedFrom":[makeQuery(id+"F1.opExtrude","CAP_FACE",FACE,{"disambiguationData":[OSD([subQ15,subQ14,subQ4,subQ7,subQ13,subQ17,subQ18,subQ19,subQ20,subQ16,subQ21,subQ12,subQ11,subQ10,subQ9,subQ8,subQ6,subQ5,subQ3,subQ2,subQ1,sQuery(id+"F0.wireOp",EDGE,"E16"),subQ0,sQuery(id+"F0.wireOp",EDGE,"E18"),sQuery(id+"F0.wireOp",EDGE,"E19"),subQ22])],"isStart":true}),makeQuery(id+"F6.opExtrude","SWEPT_FACE",FACE,{"disambiguationData":[OSD([subQ22]),TDD([makeQuery(id+"F1.opExtrude","CAP_EDGE",EDGE,{"disambiguationData":[OSD([subQ22])],"isStart":true})])]})]})}),makeQuery(id+"F21.opExtrude","SWEPT_FACE",FACE,{"disambiguationData":[OSD([sQuery(id+"F20.wireOp",EDGE,"E43.top")])]})]});}
            var sketch = newSketch(context, id + "F30", { "sketchPlane" : qUnion([Q0])});
            skLineSegment(sketch, "E46.bottom", {"start": v(-20, 26.5) * mm, "end": v(-33.05, 26.5) * mm});
            skLineSegment(sketch, "E46.top", {"start": v(-20, 17.5) * mm, "end": v(-33.05, 17.5) * mm});
            skLineSegment(sketch, "E46.left", {"start": v(-20, 26.5) * mm, "end": v(-20, 17.5) * mm});
            skLineSegment(sketch, "E46.right", {"start": v(-33.05, 26.5) * mm, "end": v(-33.05, 17.5) * mm});
            skSolve(sketch);
        }
        {
            var Q0;
            Q0 = qSketchRegion(id + "F30", true);
            extrude(context, id + "F31", {"entities" : qUnion([Q0]), "operationType" : NewBodyOperationType.REMOVE, "oppositeDirection" : true, "depth" : 25 * mm});
        }
        {
            var Q0;
            Q0=makeQuery(id+"F31.boolean.opBoolean","INTERSECT",EDGE,{"derivedFrom":[makeQuery(id+"F1.opExtrude","SWEPT_FACE",FACE,{"disambiguationData":[OSD([sQuery(id+"F0.wireOp",EDGE,"E0.left")])]}),makeQuery(id+"F31.opExtrude","SWEPT_FACE",FACE,{"disambiguationData":[OSD([sQuery(id+"F30.wireOp",EDGE,"E46.top")])]})]});
            fillet(context, id + "F32", {"entities" : qUnion([Q0]), "radius" : 8 * mm, "tangentPropagation" : true, "allowEdgeOverflow" : false});
        }
        {
            var Q0;
            Q0=qCreatedBy(makeId("Top.planeOp"),FACE);
            var sketch = newSketch(context, id + "F33", { "sketchPlane" : qUnion([Q0])});
            skLineSegment(sketch, "E47.bottom", {"start": v(-4.02, -7) * mm, "end": v(3.98, -7) * mm});
            skLineSegment(sketch, "E47.top", {"start": v(-4.02, -18) * mm, "end": v(3.98, -18) * mm});
            skLineSegment(sketch, "E47.left", {"start": v(-4.02, -7) * mm, "end": v(-4.02, -18) * mm});
            skLineSegment(sketch, "E47.right", {"start": v(3.98, -7) * mm, "end": v(3.98, -18) * mm});
            skSolve(sketch);
        }
        {
            var Q0;
            Q0 = qSketchRegion(id + "F33", true);
            var Q1;
            {var subQ0=sQuery(id+"F0.wireOp",EDGE,"E20.trimOffspring");Q1=makeQuery(id+"F21.boolean.opBoolean","MERGE",FACE,{"derivedFrom":[makeQuery(id+"F6.boolean.opBoolean","MERGE",FACE,{"derivedFrom":[makeQuery(id+"F1.opExtrude","CAP_FACE",FACE,{"disambiguationData":[OSD([sQuery(id+"F0.wireOp",EDGE,"E0.bottom"),sQuery(id+"F0.wireOp",EDGE,"E0.left"),sQuery(id+"F0.wireOp",EDGE,"E0.right"),sQuery(id+"F0.wireOp",EDGE,"E0.top"),sQuery(id+"F0.wireOp",EDGE,"E1.left"),sQuery(id+"F0.wireOp",EDGE,"E1.right"),sQuery(id+"F0.wireOp",EDGE,"E2"),sQuery(id+"F0.wireOp",EDGE,"E4"),sQuery(id+"F0.wireOp",EDGE,"E6"),sQuery(id+"F0.wireOp",EDGE,"E7"),sQuery(id+"F0.wireOp",EDGE,"E8"),sQuery(id+"F0.wireOp",EDGE,"E9.MirrorC"),sQuery(id+"F0.wireOp",EDGE,"E10.bottom"),sQuery(id+"F0.wireOp",EDGE,"E10.top"),sQuery(id+"F0.wireOp",EDGE,"E10.left"),sQuery(id+"F0.wireOp",EDGE,"E10.right"),sQuery(id+"F0.wireOp",EDGE,"E11.MirrorCS"),sQuery(id+"F0.wireOp",EDGE,"E12.MirrorCS"),sQuery(id+"F0.wireOp",EDGE,"E13.MirrorCS"),sQuery(id+"F0.wireOp",EDGE,"E14.MirrorCS"),sQuery(id+"F0.wireOp",EDGE,"E15"),sQuery(id+"F0.wireOp",EDGE,"E16"),sQuery(id+"F0.wireOp",EDGE,"E17"),sQuery(id+"F0.wireOp",EDGE,"E18"),sQuery(id+"F0.wireOp",EDGE,"E19"),subQ0])],"isStart":false}),makeQuery(id+"F6.opExtrude","SWEPT_FACE",FACE,{"disambiguationData":[OSD([subQ0]),TDD([makeQuery(id+"F1.opExtrude","CAP_EDGE",EDGE,{"disambiguationData":[OSD([subQ0])],"isStart":false})])]})]}),makeQuery(id+"F21.opExtrude","SWEPT_FACE",FACE,{"disambiguationData":[OSD([sQuery(id+"F20.wireOp",EDGE,"E43.bottom")])]})]});}
            extrude(context, id + "F34", {"entities" : qUnion([Q0]), "operationType" : NewBodyOperationType.ADD, "endBound" : BoundingType.UP_TO_SURFACE, "endBoundEntityFace" : qUnion([Q1]), "depth" : 5.1 * mm});
        }
        {
            var Q0;
            Q0=makeQuery(id+"F34.opExtrude","CAP_EDGE",EDGE,{"disambiguationData":[OSD([sQuery(id+"F33.wireOp",EDGE,"E47.bottom")])],"isStart":true});
            fillet(context, id + "F35", {"entities" : qUnion([Q0]), "radius" : 5 * mm, "tangentPropagation" : true, "allowEdgeOverflow" : false});
        }
        {
            var Q0;
            Q0=makeQuery(id+"F34.boolean.opBoolean","INTERSECT",EDGE,{"derivedFrom":[makeQuery(id+"F26.boolean.opBoolean","COPY",FACE,{"derivedFrom":makeQuery(id+"F26.opExtrude","SWEPT_FACE",FACE,{"disambiguationData":[OSD([sQuery(id+"F25.wireOp",EDGE,"E45.top")])]})}),makeQuery(id+"F34.opExtrude","SWEPT_FACE",FACE,{"disambiguationData":[OSD([sQuery(id+"F33.wireOp",EDGE,"E47.right")])]})]});
            var Q1;
            Q1=makeQuery(id+"F34.boolean.opBoolean","INTERSECT",EDGE,{"derivedFrom":[makeQuery(id+"F26.boolean.opBoolean","COPY",FACE,{"derivedFrom":makeQuery(id+"F26.opExtrude","SWEPT_FACE",FACE,{"disambiguationData":[OSD([sQuery(id+"F25.wireOp",EDGE,"E45.top")])]})}),makeQuery(id+"F34.opExtrude","SWEPT_FACE",FACE,{"disambiguationData":[OSD([sQuery(id+"F33.wireOp",EDGE,"E47.left")])]})]});
            fillet(context, id + "F36", {"entities" : qUnion([Q0, Q1]), "radius" : 2 * mm, "tangentPropagation" : true, "allowEdgeOverflow" : false});
        }
        {
            var Q0;
            Q0=makeQuery(id+"F34.boolean.opBoolean","INTERSECT",EDGE,{"derivedFrom":[makeQuery(id+"F26.boolean.opBoolean","MERGE",FACE,{"derivedFrom":[makeQuery(id+"F24.boolean.opBoolean","COPY",FACE,{"derivedFrom":makeQuery(id+"F24.opExtrude","SWEPT_FACE",FACE,{"disambiguationData":[OSD([sQuery(id+"F23.wireOp",EDGE,"E44.top")])]})})],"fromTools":[makeQuery(id+"F26.opExtrude","SWEPT_FACE",FACE,{"disambiguationData":[OSD([sQuery(id+"F25.wireOp",EDGE,"E45.bottom")])]})]}),makeQuery(id+"F34.opExtrude","SWEPT_FACE",FACE,{"disambiguationData":[OSD([sQuery(id+"F33.wireOp",EDGE,"E47.right")])]})]});
            var Q1;
            Q1=makeQuery(id+"F34.boolean.opBoolean","INTERSECT",EDGE,{"derivedFrom":[makeQuery(id+"F26.boolean.opBoolean","MERGE",FACE,{"derivedFrom":[makeQuery(id+"F24.boolean.opBoolean","COPY",FACE,{"derivedFrom":makeQuery(id+"F24.opExtrude","SWEPT_FACE",FACE,{"disambiguationData":[OSD([sQuery(id+"F23.wireOp",EDGE,"E44.top")])]})})],"fromTools":[makeQuery(id+"F26.opExtrude","SWEPT_FACE",FACE,{"disambiguationData":[OSD([sQuery(id+"F25.wireOp",EDGE,"E45.bottom")])]})]}),makeQuery(id+"F34.opExtrude","SWEPT_FACE",FACE,{"disambiguationData":[OSD([sQuery(id+"F33.wireOp",EDGE,"E47.left")])]})]});
            fillet(context, id + "F37", {"entities" : qUnion([Q0, Q1]), "radius" : 2 * mm, "tangentPropagation" : true, "allowEdgeOverflow" : false});
        }
    });
